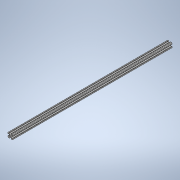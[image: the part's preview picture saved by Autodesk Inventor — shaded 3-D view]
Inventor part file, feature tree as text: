
AUTODESK INVENTOR PART (.ipt)
format: ipt  version: 2020 (Build 240168000, 168)  size: 243,200 bytes
history: native  units: in
note: dims shown in document units (in); Inventor stores cm internally (conversion verified against a paired STEP export)
features: extrude x1, sketch x1
ambient origin geometry x8: Origin, YZ Plane, XZ Plane, XY Plane, X Axis, Y Axis, Z Axis, Center Point
bodies: Solid1 (feature_tree)
feature tree (2):
  extrude  "Extrusion1"  [1 undecoded]
  sketch  "Sketch1"  dims[d0=33.0in d1=0.0in]
note: 1 required parameter value undecoded (feature->parameter linkage not recoverable at this tier; creation-order binding heuristic only, values carry confidence <= 0.55)
